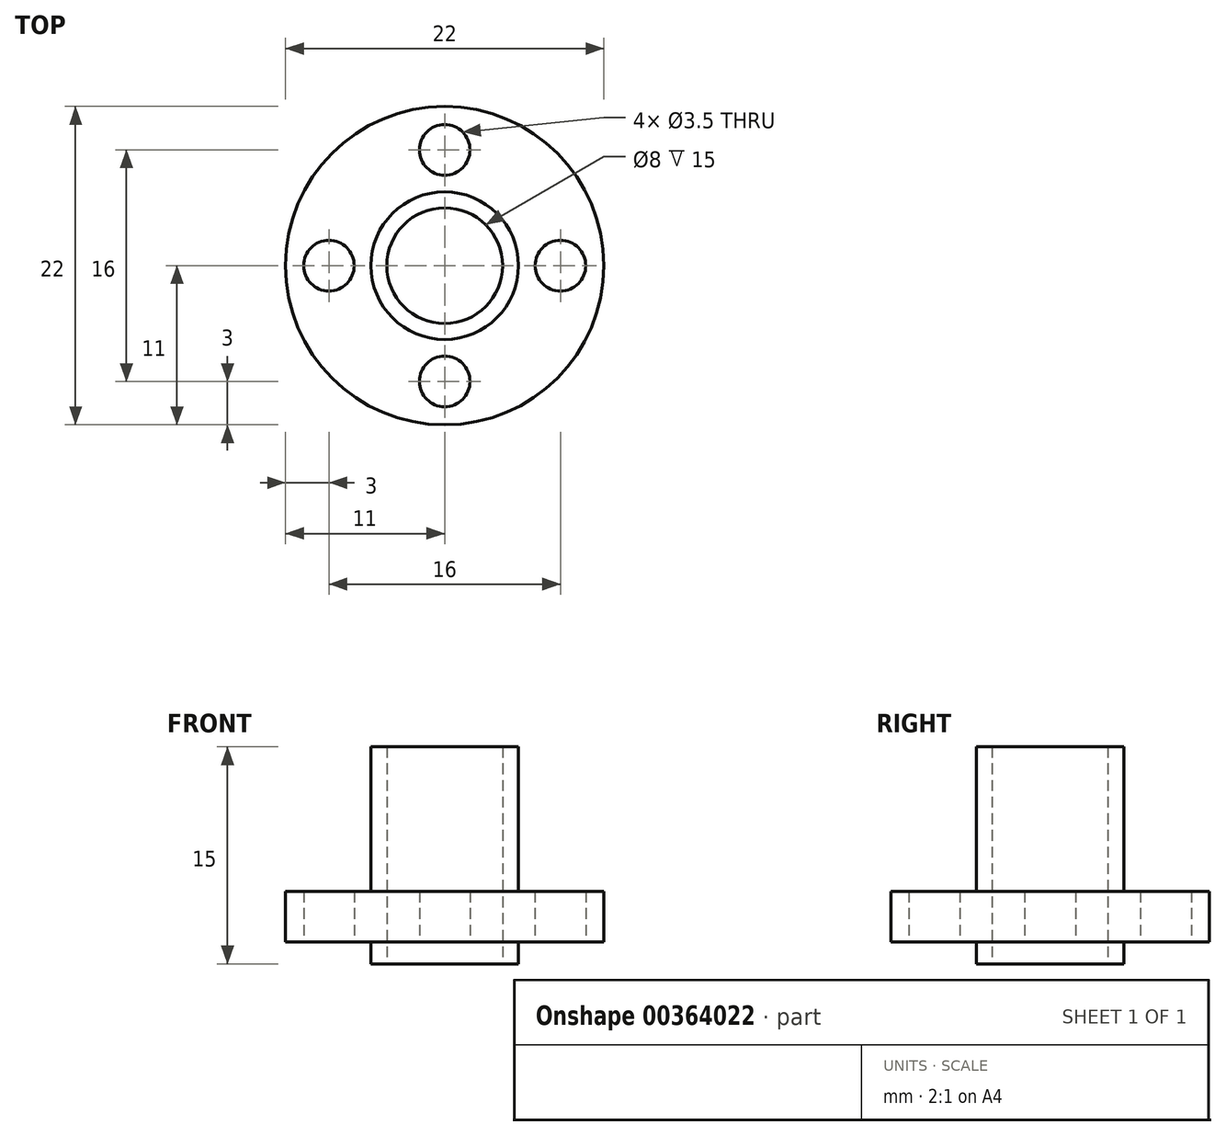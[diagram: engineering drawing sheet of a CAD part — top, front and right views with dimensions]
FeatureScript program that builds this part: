
annotation { "Feature Type Name" : "Feature", "Feature Type Description" : "" }
export const myFeature = defineFeature(function(context is Context, id is Id, definition is map)
    precondition{}
    {
        {
            var Q0;
            Q0=qCreatedBy(makeId("Top.planeOp"),FACE);
            var sketch = newSketch(context, id + "F0", { "sketchPlane" : qUnion([Q0])});
            skCircle(sketch, "E0", {"center": v(0, 0) * mm, "radius": 11 * mm});
            skCircle(sketch, "E1", {"center": v(0, 0) * mm, "radius": 4 * mm});
            skLineSegment(sketch, "E2", {"start": v(0, 0) * mm, "end": v(-8, 0) * mm, "construction": true});
            skCircle(sketch, "E3", {"center": v(-8, 0) * mm, "radius": 1.75 * mm});
            skCircle(sketch, "E4.1.0", {"center": v(0, -8) * mm, "radius": 1.75 * mm});
            skCircle(sketch, "E4.2.0", {"center": v(8, 0) * mm, "radius": 1.75 * mm});
            skCircle(sketch, "E4.3.0", {"center": v(0, 8) * mm, "radius": 1.75 * mm});
            skSolve(sketch);
        }
        {
            var Q0;
            Q0 = qSketchRegion(id + "F0", true);
            extrude(context, id + "F1", {"entities" : qUnion([Q0]), "depth" : 3.5 * mm});
        }
        {
            var Q0;
            Q0=makeQuery(id+"F1.opExtrude","CAP_FACE",FACE,{"disambiguationData":[OSD([sQuery(id+"F0.wireOp",EDGE,"E0"),sQuery(id+"F0.wireOp",EDGE,"E1"),sQuery(id+"F0.wireOp",EDGE,"E3"),sQuery(id+"F0.wireOp",EDGE,"E4.1.0"),sQuery(id+"F0.wireOp",EDGE,"E4.2.0"),sQuery(id+"F0.wireOp",EDGE,"E4.3.0")])],"isStart":false});
            var sketch = newSketch(context, id + "F2", { "sketchPlane" : qUnion([Q0])});
            skCircle(sketch, "E5", {"center": v(0, 0) * mm, "radius": 5.1 * mm});
            skCircle(sketch, "E6", {"center": v(0, 0) * mm, "radius": 4 * mm});
            skSolve(sketch);
        }
        {
            var Q0;
            Q0 = qSketchRegion(id + "F2", true);
            extrude(context, id + "F3", {"entities" : qUnion([Q0]), "operationType" : NewBodyOperationType.ADD, "depth" : 10 * mm});
        }
        {
            var Q0;
            Q0=makeQuery(id+"F1.opExtrude","CAP_FACE",FACE,{"disambiguationData":[OSD([sQuery(id+"F0.wireOp",EDGE,"E0"),sQuery(id+"F0.wireOp",EDGE,"E1"),sQuery(id+"F0.wireOp",EDGE,"E3"),sQuery(id+"F0.wireOp",EDGE,"E4.1.0"),sQuery(id+"F0.wireOp",EDGE,"E4.2.0"),sQuery(id+"F0.wireOp",EDGE,"E4.3.0")])],"isStart":true});
            var sketch = newSketch(context, id + "F4", { "sketchPlane" : qUnion([Q0])});
            skCircle(sketch, "E7", {"center": v(0, 0) * mm, "radius": 4 * mm});
            skCircle(sketch, "E8", {"center": v(0, 0) * mm, "radius": 5.1 * mm});
            skSolve(sketch);
        }
        {
            var Q0;
            Q0 = qSketchRegion(id + "F4", true);
            extrude(context, id + "F5", {"entities" : qUnion([Q0]), "operationType" : NewBodyOperationType.ADD, "depth" : 1.5 * mm});
        }
    });
